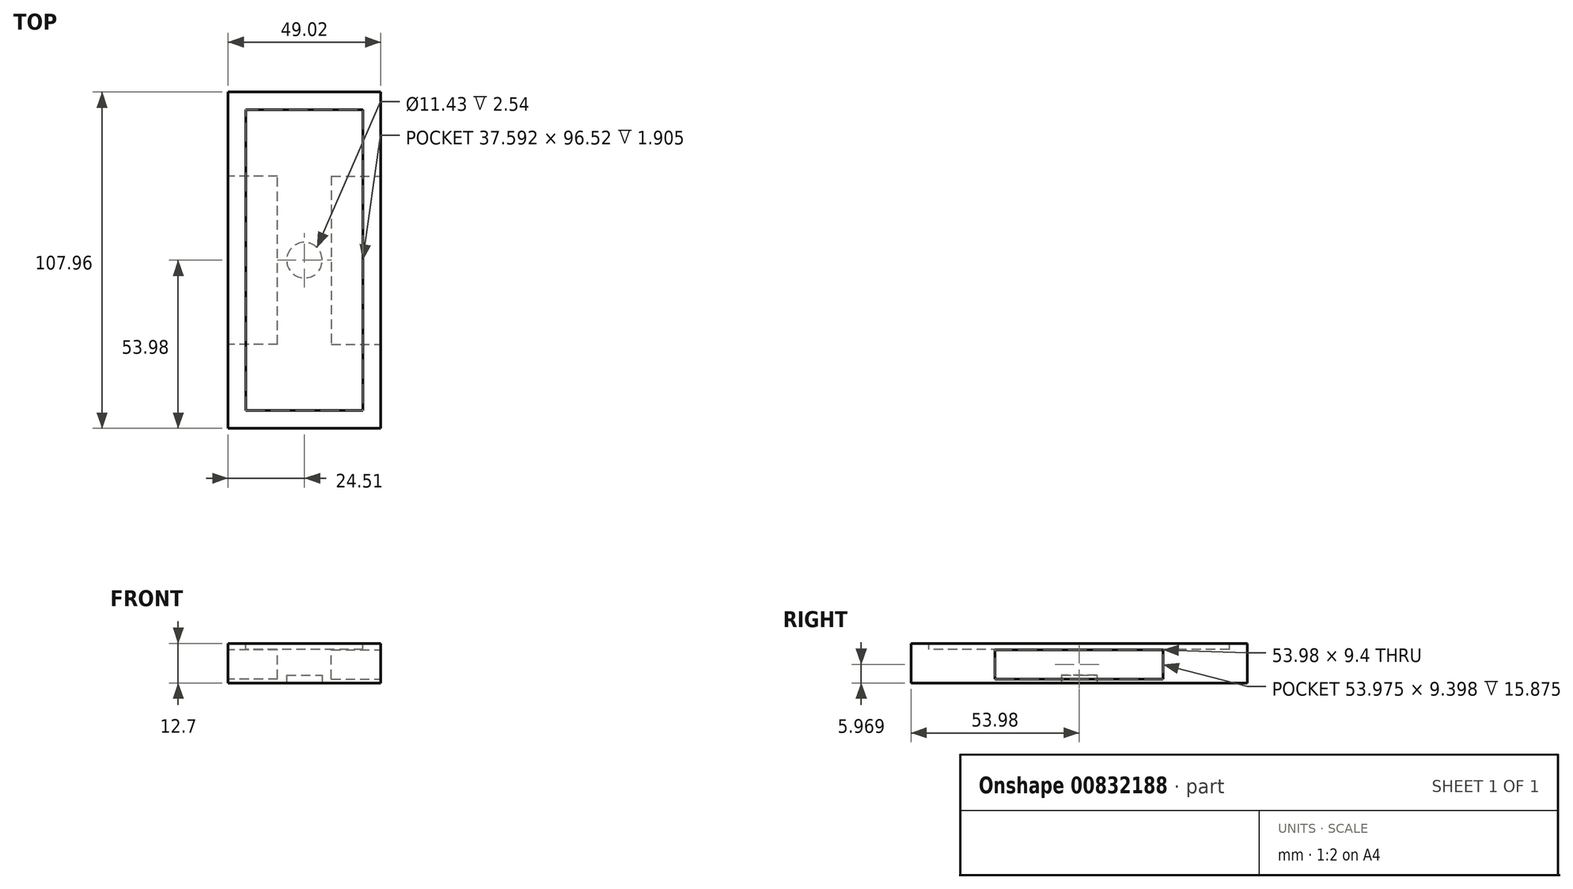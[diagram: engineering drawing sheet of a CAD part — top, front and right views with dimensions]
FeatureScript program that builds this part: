
annotation { "Feature Type Name" : "Feature", "Feature Type Description" : "" }
export const myFeature = defineFeature(function(context is Context, id is Id, definition is map)
    precondition{}
    {
        {
            var Q0;
            Q0=qCreatedBy(makeId("Top.planeOp"),FACE);
            var sketch = newSketch(context, id + "F0", { "sketchPlane" : qUnion([Q0])});
            skLineSegment(sketch, "E0.bottom", {"start": v(24.51, 53.98) * mm, "end": v(-24.51, 53.98) * mm});
            skLineSegment(sketch, "E0.top", {"start": v(24.51, -53.98) * mm, "end": v(-24.51, -53.98) * mm});
            skLineSegment(sketch, "E0.left", {"start": v(24.51, 53.98) * mm, "end": v(24.51, -53.97) * mm});
            skLineSegment(sketch, "E0.right", {"start": v(-24.51, 53.98) * mm, "end": v(-24.51, -53.98) * mm});
            skPoint(sketch, "E0.middle", {"position": v(0, 0) * mm});
            skSolve(sketch);
        }
        {
            var Q0;
            Q0=qSketchRegion(id+"F0",true);
            extrude(context, id + "F1", {"entities" : qUnion([Q0]), "depth" : 12.7 * mm, "offsetDistance" : 25.4 * mm});
        }
        {
            var Q0;
            Q0=makeQuery(id+"F1.opExtrude","CAP_FACE",FACE,{"disambiguationData":[OSD([sQuery(id+"F0.wireOp",EDGE,"E0.bottom"),sQuery(id+"F0.wireOp",EDGE,"E0.top"),sQuery(id+"F0.wireOp",EDGE,"E0.left"),sQuery(id+"F0.wireOp",EDGE,"E0.right")])],"isStart":true});
            var sketch = newSketch(context, id + "F2", { "sketchPlane" : qUnion([Q0])});
            skCircle(sketch, "E1", {"center": v(0, 0) * mm, "radius": 5.72 * mm});
            skSolve(sketch);
        }
        {
            var Q0;
            Q0=makeQuery(id+"F2.imprint","IMPRINT",FACE,{"disambiguationData":[TD([[makeQuery(id+"F2.imprint","IMPRINT",EDGE,{"derivedFrom":sQuery(id+"F2.wireOp",EDGE,"E1")}),1.0]])]});
            extrude(context, id + "F3", {"entities" : qUnion([Q0]), "operationType" : NewBodyOperationType.REMOVE, "oppositeDirection" : true, "depth" : 2.54 * mm, "offsetDistance" : 25.4 * mm});
        }
        {
            var Q0;
            Q0=makeQuery(id+"F1.opExtrude","CAP_FACE",FACE,{"disambiguationData":[OSD([sQuery(id+"F0.wireOp",EDGE,"E0.bottom"),sQuery(id+"F0.wireOp",EDGE,"E0.top"),sQuery(id+"F0.wireOp",EDGE,"E0.left"),sQuery(id+"F0.wireOp",EDGE,"E0.right")])],"isStart":false});
            var sketch = newSketch(context, id + "F4", { "sketchPlane" : qUnion([Q0])});
            skLineSegment(sketch, "E2.bottom", {"start": v(18.8, 48.26) * mm, "end": v(-18.8, 48.26) * mm});
            skLineSegment(sketch, "E2.top", {"start": v(18.8, -48.26) * mm, "end": v(-18.8, -48.26) * mm});
            skLineSegment(sketch, "E2.left", {"start": v(18.8, 48.26) * mm, "end": v(18.8, -48.26) * mm});
            skLineSegment(sketch, "E2.right", {"start": v(-18.8, 48.26) * mm, "end": v(-18.8, -48.26) * mm});
            skPoint(sketch, "E2.middle", {"position": v(0, 0) * mm});
            skSolve(sketch);
        }
        {
            var Q0;
            Q0=makeQuery(id+"F4.imprint","IMPRINT",FACE,{"disambiguationData":[TD([[makeQuery(id+"F4.imprint","IMPRINT",EDGE,{"derivedFrom":sQuery(id+"F4.wireOp",EDGE,"E2.bottom")}),1.0]])]});
            extrude(context, id + "F5", {"entities" : qUnion([Q0]), "operationType" : NewBodyOperationType.REMOVE, "oppositeDirection" : true, "depth" : 1.9 * mm, "offsetDistance" : 25.4 * mm});
        }
        {
            var Q0;
            Q0=makeQuery(id+"F1.opExtrude","SWEPT_FACE",FACE,{"disambiguationData":[OSD([sQuery(id+"F0.wireOp",EDGE,"E0.right")])]});
            var sketch = newSketch(context, id + "F6", { "sketchPlane" : qUnion([Q0])});
            skPoint(sketch, "E3.middle.positionSnap0", {"position": v(0, 0) * mm});
            skPoint(sketch, "E3.centerSnap0", {"position": v(0, 0) * mm});
            skLineSegment(sketch, "E4", {"start": v(53.97, 0) * mm, "end": v(-53.98, 0) * mm, "construction": true});
            skLineSegment(sketch, "E5", {"start": v(53.98, 12.7) * mm, "end": v(-53.98, 12.7) * mm, "construction": true});
            skLineSegment(sketch, "E6.bottom", {"start": v(26.99, 1.27) * mm, "end": v(-26.99, 1.27) * mm});
            skLineSegment(sketch, "E6.top", {"start": v(26.99, 10.67) * mm, "end": v(-26.99, 10.67) * mm});
            skLineSegment(sketch, "E6.left", {"start": v(26.99, 1.27) * mm, "end": v(26.99, 10.67) * mm});
            skLineSegment(sketch, "E6.right", {"start": v(-26.99, 1.27) * mm, "end": v(-26.99, 10.67) * mm});
            skPoint(sketch, "E6.middle", {"position": v(0, 5.97) * mm});
            skSolve(sketch);
        }
        {
            var Q0;
            Q0=makeQuery(id+"F6.imprint","IMPRINT",FACE,{"disambiguationData":[TD([[makeQuery(id+"F6.imprint","IMPRINT",EDGE,{"derivedFrom":sQuery(id+"F6.wireOp",EDGE,"E6.bottom")}),-1.0]])]});
            extrude(context, id + "F7", {"entities" : qUnion([Q0]), "operationType" : NewBodyOperationType.REMOVE, "oppositeDirection" : true, "depth" : 15.88 * mm, "offsetDistance" : 25.4 * mm});
        }
        {
            var Q0;
            Q0=makeQuery(id+"F1.opExtrude","SWEPT_FACE",FACE,{"disambiguationData":[OSD([sQuery(id+"F0.wireOp",EDGE,"E0.left")])]});
            var sketch = newSketch(context, id + "F8", { "sketchPlane" : qUnion([Q0])});
            skPoint(sketch, "E7.middle.positionSnap0", {"position": v(0, 1.59) * mm});
            skPoint(sketch, "E7.centerSnap0", {"position": v(0, 1.59) * mm});
            skLineSegment(sketch, "E8.bottom", {"start": v(26.99, 1.27) * mm, "end": v(-26.99, 1.27) * mm});
            skLineSegment(sketch, "E8.top", {"start": v(26.99, 10.67) * mm, "end": v(-26.99, 10.67) * mm});
            skLineSegment(sketch, "E8.left", {"start": v(26.99, 1.27) * mm, "end": v(26.99, 10.67) * mm});
            skLineSegment(sketch, "E8.right", {"start": v(-26.99, 1.27) * mm, "end": v(-26.99, 10.67) * mm});
            skPoint(sketch, "E8.middle", {"position": v(0, 5.97) * mm});
            skSolve(sketch);
        }
        {
            var Q0;
            Q0=makeQuery(id+"F8.imprint","IMPRINT",FACE,{"disambiguationData":[TD([[makeQuery(id+"F8.imprint","IMPRINT",EDGE,{"derivedFrom":sQuery(id+"F8.wireOp",EDGE,"E8.bottom")}),-1.0]])]});
            extrude(context, id + "F9", {"entities" : qUnion([Q0]), "operationType" : NewBodyOperationType.REMOVE, "oppositeDirection" : true, "depth" : 15.88 * mm, "offsetDistance" : 25.4 * mm});
        }
    });
